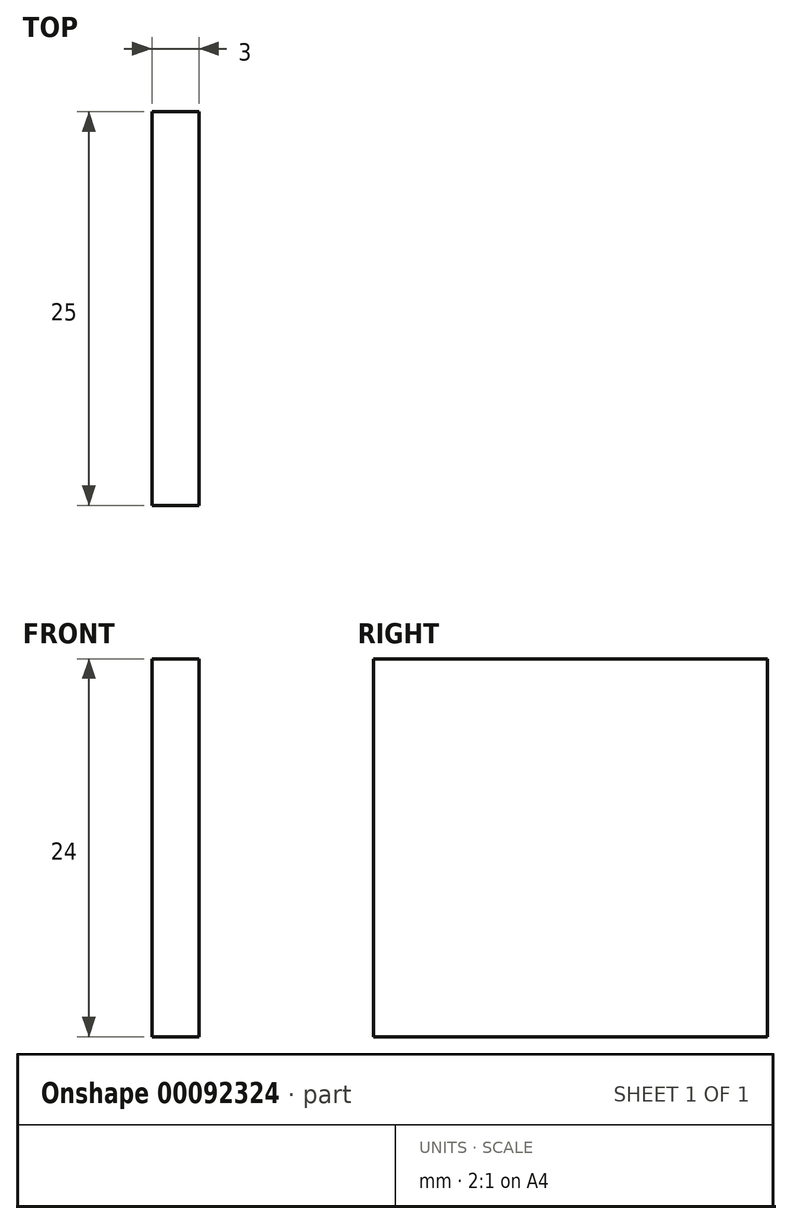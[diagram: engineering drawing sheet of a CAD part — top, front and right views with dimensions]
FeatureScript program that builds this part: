
annotation { "Feature Type Name" : "Feature", "Feature Type Description" : "" }
export const myFeature = defineFeature(function(context is Context, id is Id, definition is map)
    precondition{}
    {
        {
            var Q0;
            Q0=qCreatedBy(makeId("Right.planeOp"),FACE);
            var sketch = newSketch(context, id + "F0", { "sketchPlane" : qUnion([Q0])});
            skLineSegment(sketch, "E0.bottom", {"start": v(-12.5, 12) * mm, "end": v(12.5, 12) * mm});
            skLineSegment(sketch, "E0.top", {"start": v(-12.5, -12) * mm, "end": v(12.5, -12) * mm});
            skLineSegment(sketch, "E0.left", {"start": v(-12.5, 12) * mm, "end": v(-12.5, -12) * mm});
            skLineSegment(sketch, "E0.right", {"start": v(12.5, 12) * mm, "end": v(12.5, -12) * mm});
            skSolve(sketch);
        }
        {
            var Q0;
            Q0=makeQuery(id+"F0.imprint","IMPRINT",FACE,{"disambiguationData":[TD([[makeQuery(id+"F0.imprint","IMPRINT",EDGE,{"derivedFrom":sQuery(id+"F0.wireOp",EDGE,"E0.bottom")}),-1.0]])]});
            extrude(context, id + "F1", {"entities" : qUnion([Q0]), "endBound" : BoundingType.SYMMETRIC, "depth" : 3 * mm});
        }
    });
